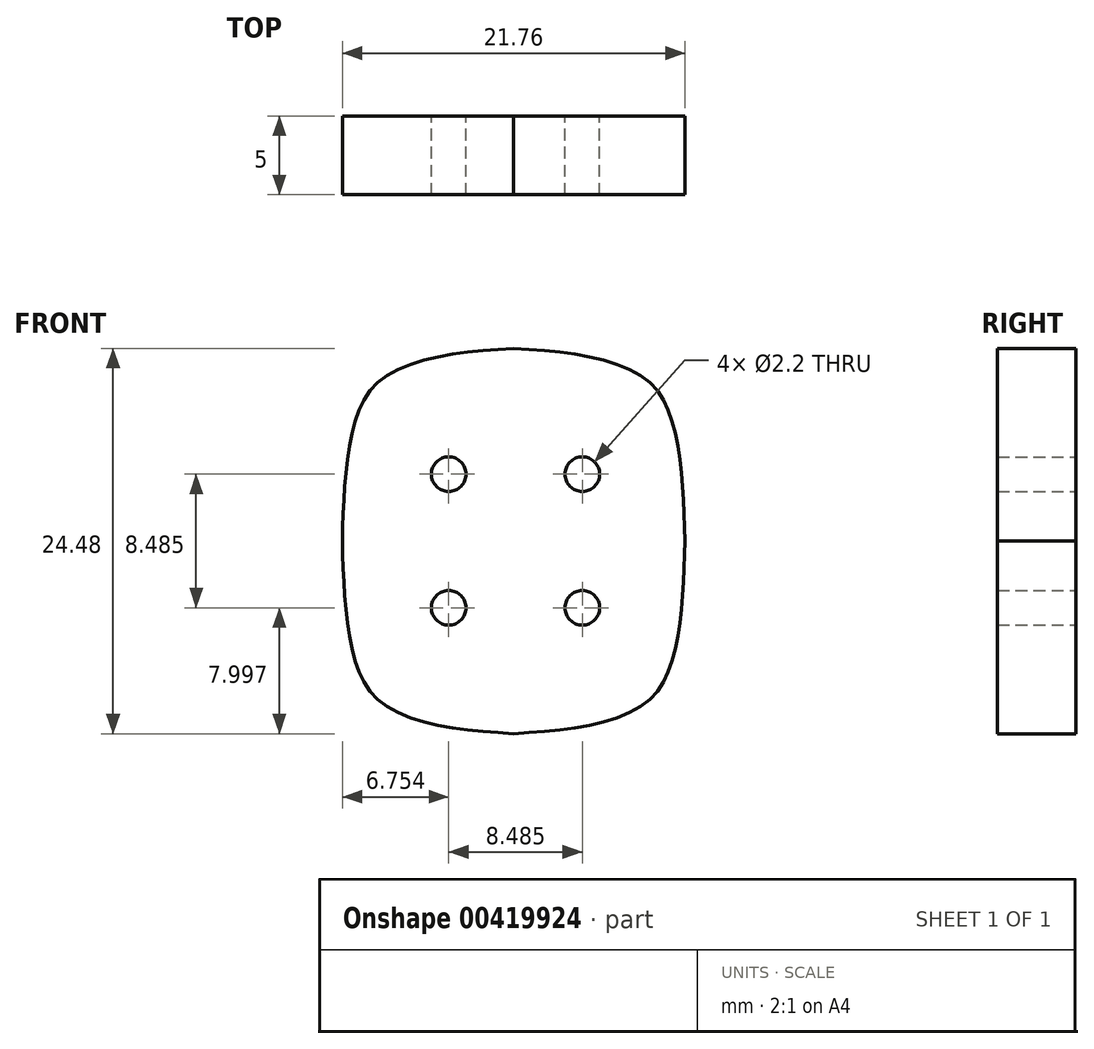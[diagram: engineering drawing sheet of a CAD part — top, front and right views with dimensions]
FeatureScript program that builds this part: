
annotation { "Feature Type Name" : "Feature", "Feature Type Description" : "" }
export const myFeature = defineFeature(function(context is Context, id is Id, definition is map)
    precondition{}
    {
        {
            var Q0;
            Q0=qCreatedBy(makeId("Front.planeOp"),FACE);
            var sketch = newSketch(context, id + "F0", { "sketchPlane" : qUnion([Q0])});
            skCircle(sketch, "E0", {"center": v(4.36, -4.24) * mm, "radius": 1.1 * mm});
            skCircle(sketch, "E1", {"center": v(-4.13, -4.24) * mm, "radius": 1.1 * mm});
            skCircle(sketch, "E2", {"center": v(-4.13, 4.24) * mm, "radius": 1.1 * mm});
            skCircle(sketch, "E3", {"center": v(4.36, 4.24) * mm, "radius": 1.1 * mm});
            skFitSpline(sketch, "E4.MirrorCS", {"points": [v(0, 12.24) * mm, v(5.07, 11.65) * mm, v(8.56, 10.14) * mm, v(10, 7.81) * mm, v(10.68, 4.11) * mm, v(10.88, 0) * mm], "startDerivative": vector(22.68, -1.58) * mm, "endDerivative": vector(0.55, -19.97) * mm});
            skFitSpline(sketch, "E5.MirrorCS", {"points": [v(0, 12.24) * mm, v(5.07, 11.65) * mm, v(8.56, 10.14) * mm, v(10, 7.81) * mm, v(10.68, 4.11) * mm, v(10.88, 0) * mm], "startDerivative": vector(22.68, -1.58) * mm, "endDerivative": vector(0.55, -19.97) * mm});
            skFitSpline(sketch, "E6.MirrorCS", {"points": [v(0, 12.24) * mm, v(-5.07, 11.65) * mm, v(-8.56, 10.14) * mm, v(-10, 7.81) * mm, v(-10.68, 4.11) * mm, v(-10.88, 0) * mm], "startDerivative": vector(-22.68, -1.58) * mm, "endDerivative": vector(-0.55, -19.97) * mm});
            skFitSpline(sketch, "E7.MirrorCS", {"points": [v(0, -12.24) * mm, v(5.07, -11.65) * mm, v(8.56, -10.14) * mm, v(10, -7.81) * mm, v(10.68, -4.11) * mm, v(10.88, 0) * mm], "startDerivative": vector(22.68, 1.58) * mm, "endDerivative": vector(0.55, 19.97) * mm});
            skFitSpline(sketch, "E8.MirrorCS", {"points": [v(0, -12.24) * mm, v(-5.07, -11.65) * mm, v(-8.56, -10.14) * mm, v(-10, -7.81) * mm, v(-10.68, -4.11) * mm, v(-10.88, 0) * mm], "startDerivative": vector(-22.68, 1.58) * mm, "endDerivative": vector(-0.55, 19.97) * mm});
            skSolve(sketch);
        }
        {
            var Q0;
            Q0 = qSketchRegion(id + "F0", true);
            extrude(context, id + "F1", {"entities" : qUnion([Q0]), "depth" : 5 * mm});
        }
    });
